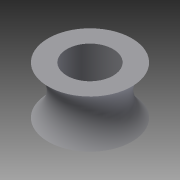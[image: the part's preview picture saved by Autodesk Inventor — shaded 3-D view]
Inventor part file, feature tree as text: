
AUTODESK INVENTOR PART (.ipt)
format: ipt  version: 2015 (Build 190159000, 159)  size: 137,728 bytes
history: native  units: in
note: dims shown in document units (in); Inventor stores cm internally (conversion verified against a paired STEP export)
features: sketch x3, extrude x2, revolve x1
ambient origin geometry x8: Origin, YZ Plane, XZ Plane, XY Plane, X Axis, Y Axis, Z Axis, Center Point
bodies: Solid1 (feature_tree)
feature tree (6):
  revolve  "Revolution1"  [1 undecoded]
  extrude  "Extrusion1"  Depth=0.28in
  extrude  "Extrusion2"  Depth=0.0551in
  sketch  "Sketch1"  dims[d0=90.0deg d1=0.32in]
  sketch  "Sketch2"  dims[d2=0.28in d3=0.4331in]
  sketch  "Sketch3"  dims[d4=0.0551in d5=0.0in d6=0.3091in d7=0.0551in d8=0.0in]
note: 1 required parameter value undecoded (feature->parameter linkage not recoverable at this tier; creation-order binding heuristic only, values carry confidence <= 0.55)
